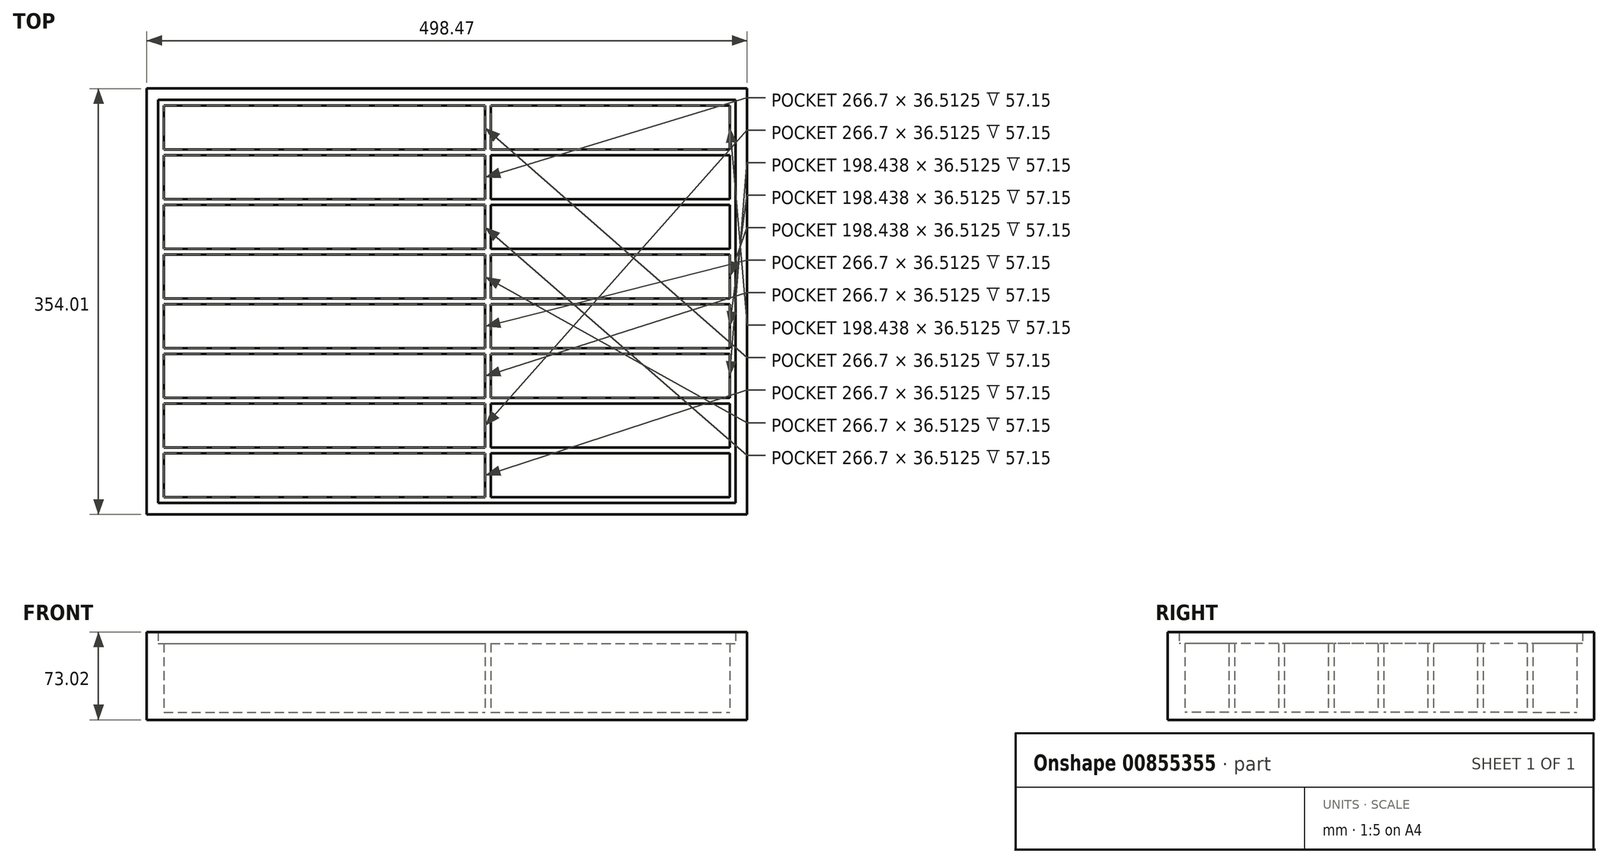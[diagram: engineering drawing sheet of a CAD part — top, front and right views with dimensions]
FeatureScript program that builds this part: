
annotation { "Feature Type Name" : "Feature", "Feature Type Description" : "" }
export const myFeature = defineFeature(function(context is Context, id is Id, definition is map)
    precondition{}
    {
        {
            var Q0;
            Q0=qCreatedBy(makeId("Top.planeOp"),FACE);
            var sketch = newSketch(context, id + "F0", { "sketchPlane" : qUnion([Q0])});
            skLineSegment(sketch, "E0.bottom", {"start": v(-260.04, 195.24) * mm, "end": v(238.43, 195.24) * mm});
            skLineSegment(sketch, "E0.top", {"start": v(-260.04, -158.77) * mm, "end": v(238.43, -158.77) * mm});
            skLineSegment(sketch, "E0.left", {"start": v(-260.04, 195.24) * mm, "end": v(-260.04, -158.77) * mm});
            skLineSegment(sketch, "E0.right", {"start": v(238.43, 195.24) * mm, "end": v(238.43, -158.77) * mm});
            skLineSegment(sketch, "E1.0", {"start": v(-250.52, 185.72) * mm, "end": v(-250.52, -149.24) * mm});
            skLineSegment(sketch, "E1.1", {"start": v(-250.52, 185.72) * mm, "end": v(228.9, 185.72) * mm});
            skLineSegment(sketch, "E1.2", {"start": v(228.9, 185.72) * mm, "end": v(228.9, -149.24) * mm});
            skLineSegment(sketch, "E1.3", {"start": v(-250.52, -149.24) * mm, "end": v(228.9, -149.24) * mm});
            skLineSegment(sketch, "E2.0", {"start": v(-245.75, 180.96) * mm, "end": v(20.95, 180.96) * mm});
            skLineSegment(sketch, "E2.1", {"start": v(-245.75, 180.96) * mm, "end": v(-245.75, 144.44) * mm});
            skLineSegment(sketch, "E2.2", {"start": v(-245.75, -144.48) * mm, "end": v(20.95, -144.48) * mm});
            skLineSegment(sketch, "E2.3", {"start": v(224.15, 180.96) * mm, "end": v(224.15, 144.44) * mm});
            skLineSegment(sketch, "E3", {"start": v(-245.75, -103.2) * mm, "end": v(20.95, -103.2) * mm});
            skLineSegment(sketch, "E4.0", {"start": v(-245.75, -107.97) * mm, "end": v(20.95, -107.97) * mm});
            skLineSegment(sketch, "E5", {"start": v(25.7, -107.97) * mm, "end": v(25.7, -144.48) * mm});
            skLineSegment(sketch, "E6.0", {"start": v(20.95, -107.97) * mm, "end": v(20.95, -144.48) * mm});
            skLineSegment(sketch, "E7.trimOffspring", {"start": v(25.7, -107.97) * mm, "end": v(224.15, -107.97) * mm});
            skLineSegment(sketch, "E8.trimOffspring", {"start": v(25.7, -103.2) * mm, "end": v(224.15, -103.2) * mm});
            skLineSegment(sketch, "E9.0.1.0", {"start": v(-245.75, -66.7) * mm, "end": v(20.95, -66.7) * mm});
            skLineSegment(sketch, "E9.0.1.1", {"start": v(-245.75, -61.93) * mm, "end": v(20.95, -61.93) * mm});
            skLineSegment(sketch, "E9.0.1.2", {"start": v(25.7, -66.7) * mm, "end": v(224.15, -66.7) * mm});
            skLineSegment(sketch, "E9.0.1.3", {"start": v(25.7, -61.93) * mm, "end": v(224.15, -61.93) * mm});
            skLineSegment(sketch, "E9.0.1.4", {"start": v(25.7, -66.7) * mm, "end": v(25.7, -103.2) * mm});
            skLineSegment(sketch, "E9.0.1.5", {"start": v(20.95, -66.7) * mm, "end": v(20.95, -103.2) * mm});
            skLineSegment(sketch, "E9.0.2.0", {"start": v(-245.75, -25.42) * mm, "end": v(20.95, -25.42) * mm});
            skLineSegment(sketch, "E9.0.2.1", {"start": v(-245.75, -20.66) * mm, "end": v(20.95, -20.66) * mm});
            skLineSegment(sketch, "E9.0.2.2", {"start": v(25.7, -25.42) * mm, "end": v(224.15, -25.42) * mm});
            skLineSegment(sketch, "E9.0.2.3", {"start": v(25.7, -20.66) * mm, "end": v(224.15, -20.66) * mm});
            skLineSegment(sketch, "E9.0.2.4", {"start": v(25.7, -25.42) * mm, "end": v(25.7, -61.93) * mm});
            skLineSegment(sketch, "E9.0.2.5", {"start": v(20.95, -25.42) * mm, "end": v(20.95, -61.93) * mm});
            skLineSegment(sketch, "E9.0.3.0", {"start": v(-245.75, 15.86) * mm, "end": v(20.95, 15.86) * mm});
            skLineSegment(sketch, "E9.0.3.1", {"start": v(-245.75, 20.62) * mm, "end": v(20.95, 20.62) * mm});
            skLineSegment(sketch, "E9.0.3.2", {"start": v(25.7, 15.86) * mm, "end": v(224.15, 15.86) * mm});
            skLineSegment(sketch, "E9.0.3.3", {"start": v(25.7, 20.62) * mm, "end": v(224.15, 20.62) * mm});
            skLineSegment(sketch, "E9.0.3.4", {"start": v(25.7, 15.86) * mm, "end": v(25.7, -20.66) * mm});
            skLineSegment(sketch, "E9.0.3.5", {"start": v(20.95, 15.86) * mm, "end": v(20.95, -20.66) * mm});
            skLineSegment(sketch, "E9.0.4.0", {"start": v(-245.75, 57.13) * mm, "end": v(20.95, 57.13) * mm});
            skLineSegment(sketch, "E9.0.4.1", {"start": v(-245.75, 61.9) * mm, "end": v(20.95, 61.9) * mm});
            skLineSegment(sketch, "E9.0.4.2", {"start": v(25.7, 57.13) * mm, "end": v(224.15, 57.13) * mm});
            skLineSegment(sketch, "E9.0.4.3", {"start": v(25.7, 61.9) * mm, "end": v(224.15, 61.9) * mm});
            skLineSegment(sketch, "E9.0.4.4", {"start": v(25.7, 57.13) * mm, "end": v(25.7, 20.62) * mm});
            skLineSegment(sketch, "E9.0.4.5", {"start": v(20.95, 57.13) * mm, "end": v(20.95, 20.62) * mm});
            skLineSegment(sketch, "E9.0.5.0", {"start": v(-245.75, 98.4) * mm, "end": v(20.95, 98.4) * mm});
            skLineSegment(sketch, "E9.0.5.1", {"start": v(-245.75, 103.17) * mm, "end": v(20.95, 103.17) * mm});
            skLineSegment(sketch, "E9.0.5.2", {"start": v(25.7, 98.4) * mm, "end": v(224.15, 98.4) * mm});
            skLineSegment(sketch, "E9.0.5.3", {"start": v(25.7, 103.17) * mm, "end": v(224.15, 103.17) * mm});
            skLineSegment(sketch, "E9.0.5.4", {"start": v(25.7, 98.4) * mm, "end": v(25.7, 61.9) * mm});
            skLineSegment(sketch, "E9.0.5.5", {"start": v(20.95, 98.4) * mm, "end": v(20.95, 61.9) * mm});
            skLineSegment(sketch, "E9.0.6.0", {"start": v(-245.75, 139.68) * mm, "end": v(20.95, 139.68) * mm});
            skLineSegment(sketch, "E9.0.6.1", {"start": v(-245.75, 144.44) * mm, "end": v(20.95, 144.44) * mm});
            skLineSegment(sketch, "E9.0.6.2", {"start": v(25.7, 139.68) * mm, "end": v(224.15, 139.68) * mm});
            skLineSegment(sketch, "E9.0.6.3", {"start": v(25.7, 144.44) * mm, "end": v(224.15, 144.44) * mm});
            skLineSegment(sketch, "E9.0.6.4", {"start": v(25.7, 139.68) * mm, "end": v(25.7, 103.17) * mm});
            skLineSegment(sketch, "E9.0.6.5", {"start": v(20.95, 139.68) * mm, "end": v(20.95, 103.17) * mm});
            skLineSegment(sketch, "E9.direction1", {"start": v(-245.75, -107.97) * mm, "end": v(-225.35, -107.97) * mm, "construction": true});
            skLineSegment(sketch, "E9.direction2", {"start": v(-245.75, -103.2) * mm, "end": v(-245.75, -66.7) * mm, "construction": true});
            skLineSegment(sketch, "E10", {"start": v(20.95, 144.44) * mm, "end": v(20.95, 180.96) * mm});
            skLineSegment(sketch, "E11", {"start": v(25.7, 144.44) * mm, "end": v(25.7, 180.96) * mm});
            skLineSegment(sketch, "E12.trimOffspring", {"start": v(25.7, 180.96) * mm, "end": v(224.15, 180.96) * mm});
            skLineSegment(sketch, "E13.trimOffspring", {"start": v(-245.75, -66.7) * mm, "end": v(-245.75, -144.48) * mm});
            skLineSegment(sketch, "E14.trimOffspring", {"start": v(-245.75, -25.42) * mm, "end": v(-245.75, -61.93) * mm});
            skLineSegment(sketch, "E15.trimOffspring", {"start": v(25.7, -144.48) * mm, "end": v(224.15, -144.48) * mm});
            skLineSegment(sketch, "E16.trimOffspring", {"start": v(-245.75, 15.86) * mm, "end": v(-245.75, -20.66) * mm});
            skLineSegment(sketch, "E17.trimOffspring", {"start": v(-245.75, 139.68) * mm, "end": v(-245.75, 20.62) * mm});
            skLineSegment(sketch, "E18.trimOffspring", {"start": v(224.15, 139.68) * mm, "end": v(224.15, 103.17) * mm});
            skLineSegment(sketch, "E19.trimOffspring", {"start": v(224.15, 98.4) * mm, "end": v(224.15, 61.9) * mm});
            skLineSegment(sketch, "E20.trimOffspring", {"start": v(224.15, -107.97) * mm, "end": v(224.15, -144.48) * mm});
            skLineSegment(sketch, "E21.trimOffspring", {"start": v(224.15, -66.7) * mm, "end": v(224.15, -103.2) * mm});
            skLineSegment(sketch, "E22.trimOffspring", {"start": v(224.15, -25.42) * mm, "end": v(224.15, -61.93) * mm});
            skLineSegment(sketch, "E23.trimOffspring", {"start": v(224.15, 15.86) * mm, "end": v(224.15, -20.66) * mm});
            skLineSegment(sketch, "E24.trimOffspring", {"start": v(224.15, 57.13) * mm, "end": v(224.15, 20.62) * mm});
            skSolve(sketch);
        }
        {
            var Q0;
            Q0=makeQuery(id+"F0.imprint","IMPRINT",FACE,{"disambiguationData":[TD([[makeQuery(id+"F0.imprint","IMPRINT",EDGE,{"derivedFrom":sQuery(id+"F0.wireOp",EDGE,"E0.bottom")}),-1.0]])]});
            extrude(context, id + "F1", {"entities" : qUnion([Q0]), "depth" : 66.67 * mm, "offsetDistance" : 25.4 * mm});
        }
        {
            var Q0;
            Q0=makeQuery(id+"F0.imprint","IMPRINT",FACE,{"disambiguationData":[TD([[makeQuery(id+"F0.imprint","IMPRINT",EDGE,{"derivedFrom":sQuery(id+"F0.wireOp",EDGE,"E1.0")}),1.0]])]});
            extrude(context, id + "F2", {"entities" : qUnion([Q0]), "depth" : 57.15 * mm, "offsetDistance" : 25.4 * mm});
        }
        {
            var Q0;
            Q0=makeQuery(id+"F0.imprint","IMPRINT",FACE,{"disambiguationData":[TD([[makeQuery(id+"F0.imprint","IMPRINT",EDGE,{"derivedFrom":sQuery(id+"F0.wireOp",EDGE,"E0.bottom")}),-1.0]])]});
            var sketch = newSketch(context, id + "F3", { "sketchPlane" : qUnion([Q0])});
            skLineSegment(sketch, "E25.0", {"start": v(-260.04, -158.77) * mm, "end": v(238.43, -158.77) * mm});
            skLineSegment(sketch, "E26.0", {"start": v(238.43, 195.24) * mm, "end": v(238.43, -158.77) * mm});
            skLineSegment(sketch, "E27.0", {"start": v(-260.04, 195.24) * mm, "end": v(238.43, 195.24) * mm});
            skLineSegment(sketch, "E28.0", {"start": v(-260.04, 195.24) * mm, "end": v(-260.04, -158.77) * mm});
            skLineSegment(sketch, "E29.left", {"start": v(-260.04, -158.77) * mm, "end": v(-260.04, 195.24) * mm});
            skLineSegment(sketch, "E29.right", {"start": v(238.43, -158.77) * mm, "end": v(238.43, 195.24) * mm});
            skSolve(sketch);
        }
        {
            var Q0;
            Q0 = qSketchRegion(id + "F3", true);
            extrude(context, id + "F4", {"entities" : qUnion([Q0]), "operationType" : NewBodyOperationType.ADD, "oppositeDirection" : true, "depth" : 6.35 * mm, "offsetDistance" : 25.4 * mm});
        }
    });
